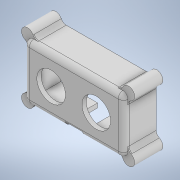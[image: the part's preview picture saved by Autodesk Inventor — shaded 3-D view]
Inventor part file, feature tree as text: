
AUTODESK INVENTOR PART (.ipt)
format: ipt  version: 2020 (Build 240168000, 168)  size: 384,000 bytes
history: native  units: in
note: dims shown in document units (in); Inventor stores cm internally (conversion verified against a paired STEP export)
features: extrude x7, sketch x6, fillet x2, plane x2, mirror x2, projected_geometry x2
ambient origin geometry x8: Origin, YZ Plane, XZ Plane, XY Plane, X Axis, Y Axis, Z Axis, Center Point
bodies: Solid1 (feature_tree)
feature tree (21):
  extrude  "Extrusion1"  Depth=0.66in
  sketch  "Sketch3"  dims[d2=0.38in d4=0.85in]
  extrude  "Extrusion2"  Depth=0.85in
  extrude  "Extrusion3"  Depth=0.41in
  fillet  "Fillet1"  Radius=0.41in
  extrude  "Extrusion4"  Depth=0.1in
  extrude  "Extrusion5"  Depth=0.65in TaperAngle=0.0deg
  extrude  "Extrusion6"  Depth=0.125in
  extrude  "Extrusion7"  Depth=0.125in
  plane  "Work Plane1"
  plane  "Work Plane2"
  mirror  "Mirror1"
  mirror  "Mirror2"
  fillet  "Fillet2"  Radius=1.09in
  sketch  "Sketch2"  dims[d0=0.66in d1=0.66in]
  projected_geometry  "Projected Loop1"
  sketch  "Sketch4"  dims[d5=0.43in d6=0.41in d7=0.41in]
  sketch  "Sketch5"  dims[d8=0.1in d9=0.0in d11=0.1in]
  projected_geometry  "Projected Loop2"
  sketch  "Sketch6"  dims[d12=0.12in d13=0.65in d14=0.0in]
  sketch  "Sketch7"  dims[d15=1.25in d16=0.0in d17=0.125in d18=0.6in d19=1.09in d20=0.0in d21=0.597in d22=0.0in d23=0.1094in d24=0.14in d25=0.65in d26=0.0in d27=0.05in d28=0.0in d29=0.125in d30=0.4in]
